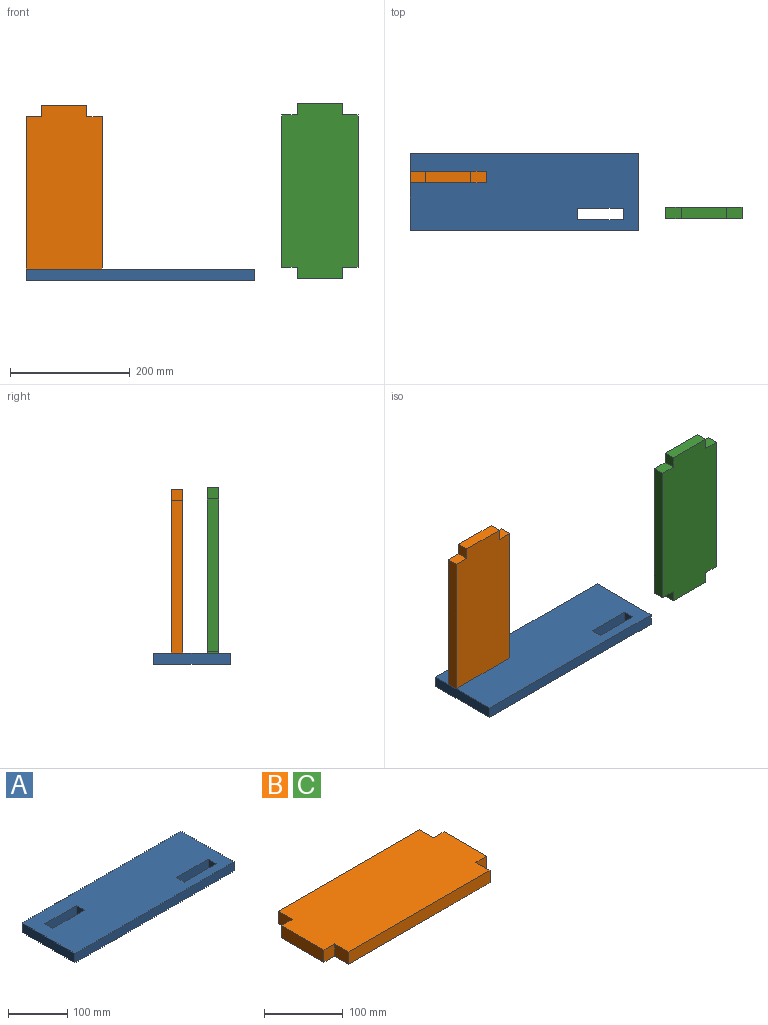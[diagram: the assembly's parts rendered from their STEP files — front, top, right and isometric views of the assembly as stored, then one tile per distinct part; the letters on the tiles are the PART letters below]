
ASSEMBLY  parts=3 mates=1
PART A: 14 faces, bbox 381x127x19.1 mm
  f0: plane 381x127mm, normal (0,0,1), area 45483.8mm2, adj f2,f3,f4,f5,f6,f7,f8,f9
  f1: plane 381x127mm, normal (0,0,-1), area 45483.8mm2, adj f2,f3,f4,f5,f6,f7,f8,f9
  f2: plane 127x19.05mm, normal (-1,0,0), area 2419.3mm2, adj f0,f1,f3,f5
  f3: plane 381x19.05mm, normal (0,-1,0), area 7258mm2, adj f0,f1,f2,f4
  f4: plane 127x19.05mm, normal (1,0,0), area 2419.3mm2, adj f0,f1,f3,f5
  f5: plane 381x19.05mm, normal (0,1,0), area 7258mm2, adj f0,f1,f2,f4
  f6: plane 76.2x19.05mm, normal (0,-1,0), area 1451.6mm2, adj f0,f1,f7,f9
  f7: plane 19.05x19.05mm, normal (1,0,0), area 362.9mm2, adj f0,f1,f6,f8
  f8: plane 76.2x19.05mm, normal (0,1,0), area 1451.6mm2, adj f0,f1,f7,f9
  f9: plane 19.05x19.05mm, normal (-1,0,0), area 362.9mm2, adj f0,f1,f6,f8
  f10: plane 76.2x19.05mm, normal (0,-1,0), area 1451.6mm2, adj f0,f1,f11,f13
  f11: plane 19.05x19.05mm, normal (1,0,0), area 362.9mm2, adj f0,f1,f10,f12
  f12: plane 76.2x19.05mm, normal (0,1,0), area 1451.6mm2, adj f0,f1,f11,f13
  f13: plane 19.05x19.05mm, normal (-1,0,0), area 362.9mm2, adj f0,f1,f10,f12
PART B: 14 faces, bbox 292.1x127x19.1 mm
  f0: plane 19.05x19.05mm, normal (0,1,0), area 362.9mm2, adj f1,f11,f12,f13
  f1: plane 76.2x19.05mm, normal (-1,0,0), area 1451.6mm2, adj f0,f2,f12,f13
  f2: plane 19.05x19.05mm, normal (0,-1,0), area 362.9mm2, adj f1,f3,f12,f13
  f3: plane 25.4x19.05mm, normal (-1,0,0), area 483.9mm2, adj f2,f4,f12,f13
  f4: plane 254x19.05mm, normal (0,-1,0), area 4838.7mm2, adj f3,f5,f12,f13
  f5: plane 25.4x19.05mm, normal (1,0,0), area 483.9mm2, adj f4,f6,f12,f13
  f6: plane 19.05x19.05mm, normal (0,-1,0), area 362.9mm2, adj f5,f7,f12,f13
  f7: plane 76.2x19.05mm, normal (1,0,0), area 1451.6mm2, adj f6,f8,f12,f13
  f8: plane 19.05x19.05mm, normal (0,1,0), area 362.9mm2, adj f7,f9,f12,f13
  f9: plane 25.4x19.05mm, normal (1,0,0), area 483.9mm2, adj f8,f10,f12,f13
  f10: plane 254x19.05mm, normal (0,1,0), area 4838.7mm2, adj f9,f11,f12,f13
  f11: plane 25.4x19.05mm, normal (-1,0,0), area 483.9mm2, adj f0,f10,f12,f13
  f12: plane 292.1x127mm, normal (0,0,1), area 35161.2mm2, adj f0,f1,f2,f3,f4,f5,f6,f7
  f13: plane 292.1x127mm, normal (0,0,-1), area 35161.2mm2, adj f0,f1,f2,f3,f4,f5,f6,f7
PART C: same geometry as B
PLACE A t=(-241.27,170.72,27.59)mm
PLACE B rot(axis=(0.58,-0.58,0.58),120deg) t=(-215.44,245.08,120.45)mm
PLACE C rot(axis=(0.58,0.58,-0.58),120deg) t=(168.19,184.99,229.68)mm
MATE fastened A.f0 <-> B.f11  axis (0,0,1) through (-275.1,245.08,46.64)mm
